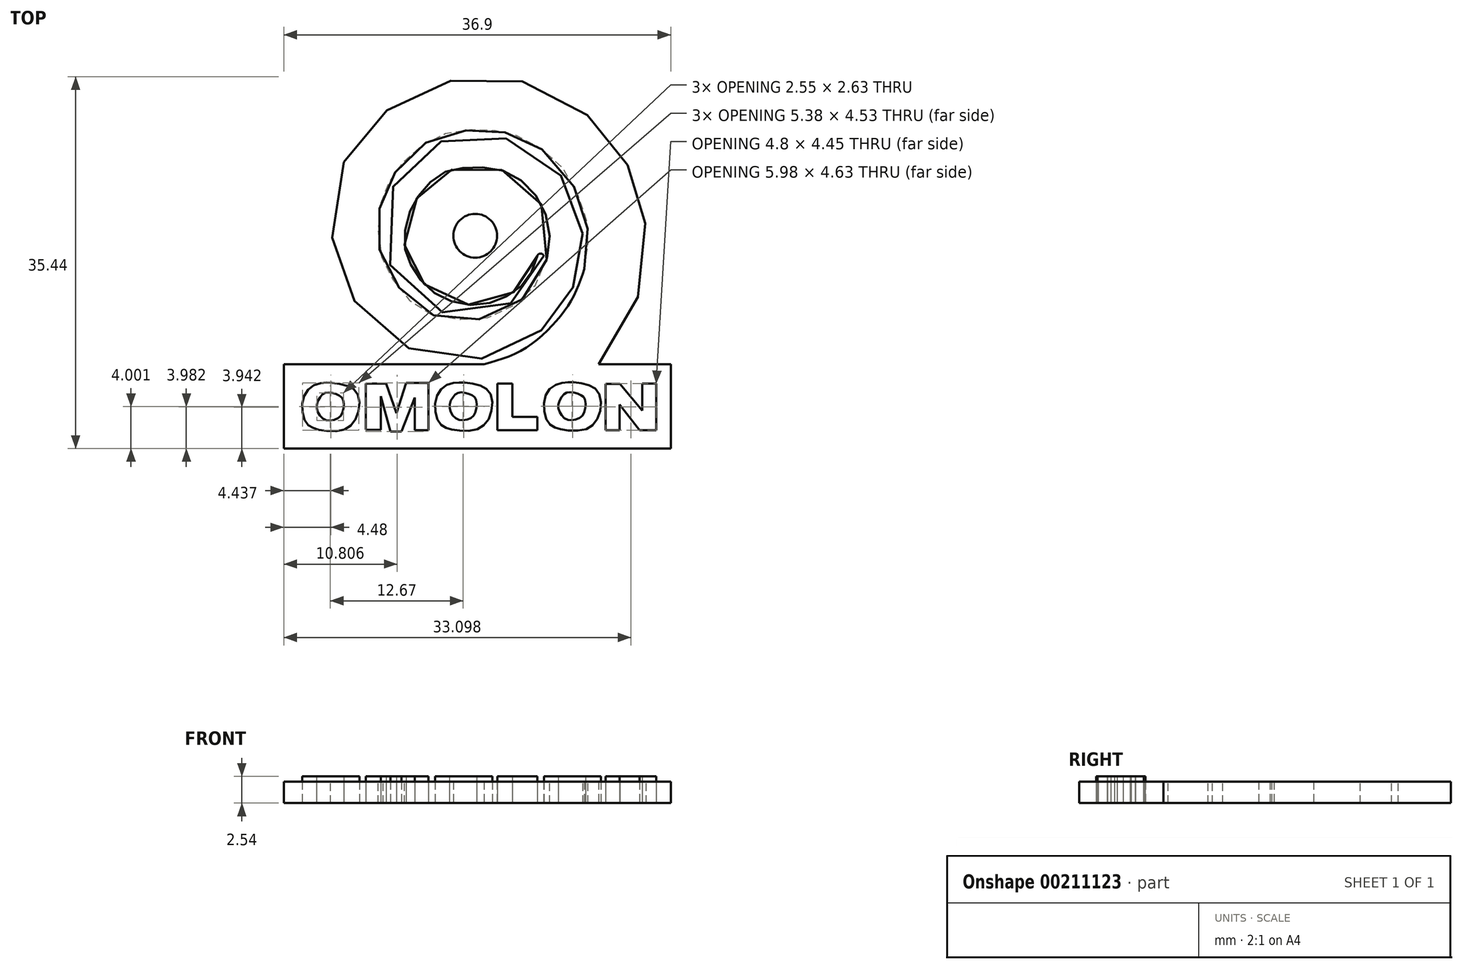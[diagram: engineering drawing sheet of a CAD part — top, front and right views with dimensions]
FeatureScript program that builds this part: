
annotation { "Feature Type Name" : "Feature", "Feature Type Description" : "" }
export const myFeature = defineFeature(function(context is Context, id is Id, definition is map)
    precondition{}
    {
        {
            var Q0;
            Q0=qCreatedBy(makeId("Top.planeOp"),FACE);
            var sketch = newSketch(context, id + "F0", { "sketchPlane" : qUnion([Q0])});
            skLineSegment(sketch, "E0.bottom", {"start": v(15, 8.8) * mm, "end": v(51.89, 8.8) * mm});
            skLineSegment(sketch, "E0.top", {"start": v(15, 0.75) * mm, "end": v(51.89, 0.75) * mm});
            skLineSegment(sketch, "E0.left", {"start": v(15, 8.8) * mm, "end": v(15, 0.75) * mm});
            skLineSegment(sketch, "E0.right", {"start": v(51.89, 8.8) * mm, "end": v(51.89, 0.75) * mm});
            skFitSpline(sketch, "E1", {"points": [v(34.07, 8.8) * mm, v(37.55, 10.04) * mm, v(40.6, 12.5) * mm, v(42.57, 15.18) * mm, v(43.65, 17.88) * mm], "startDerivative": vector(13.76, 3.77) * mm, "endDerivative": vector(4.03, 11.91) * mm});
            skFitSpline(sketch, "E2", {"points": [v(43.65, 17.88) * mm, v(43.94, 19.57) * mm, v(43.97, 21.74) * mm, v(43.65, 23.34) * mm, v(42.44, 26.15) * mm, v(40.7, 28.46) * mm, v(38.38, 29.96) * mm, v(36.75, 30.74) * mm, v(35.25, 31.02) * mm, v(33.55, 31.17) * mm, v(31.27, 30.92) * mm, v(29.35, 30.38) * mm, v(27.35, 28.96) * mm, v(25.9, 27.5) * mm, v(24.97, 26.04) * mm, v(24.22, 24.3) * mm, v(24.04, 22.13) * mm, v(24, 20.35) * mm, v(24.76, 17.88) * mm, v(25.79, 16.33) * mm, v(27.32, 14.55) * mm, v(29.42, 13.4) * mm, v(32.02, 13.05) * mm, v(34.3, 13.2) * mm, v(36.93, 14.37) * mm, v(38.81, 16.11) * mm, v(39.99, 18.5) * mm, v(40.2, 22.27) * mm, v(38.56, 25.4) * mm, v(35.9, 27.25) * mm, v(32.62, 27.54) * mm, v(30.2, 27.04) * mm, v(28.2, 25.3) * mm, v(27, 23.3) * mm, v(26.5, 20.28) * mm, v(27.14, 18.21) * mm, v(28.7, 16.11) * mm, v(31.13, 14.73) * mm, v(34.08, 14.51) * mm, v(36.5, 15.4) * mm, v(38.28, 17) * mm, v(39.17, 19.1) * mm], "startDerivative": vector(16.2, 77.75) * mm, "endDerivative": vector(29.34, 92.95) * mm});
            skFitSpline(sketch, "E3", {"points": [v(39.78, 19.1) * mm, v(39.37, 18) * mm, v(38.54, 16.46) * mm, v(37.25, 15.08) * mm, v(35.63, 14.04) * mm, v(33.6, 13.56) * mm, v(30.94, 13.54) * mm, v(27.94, 14.72) * mm, v(26.2, 16.38) * mm, v(25.15, 18.2) * mm, v(24.49, 21.47) * mm, v(24.8, 24.4) * mm, v(26.1, 26.84) * mm, v(27.37, 28.41) * mm, v(29.23, 29.68) * mm, v(30.85, 30.3) * mm, v(32.84, 30.5) * mm, v(35.1, 30.5) * mm, v(37.16, 30) * mm, v(39.17, 28.97) * mm, v(40.61, 27.72) * mm, v(42.22, 25.62) * mm, v(42.89, 24.22) * mm, v(43.35, 22.56) * mm, v(43.5, 20.7) * mm, v(43.46, 19.6) * mm, v(43.25, 18.14) * mm, v(42.7, 16.44) * mm, v(42.26, 15.49) * mm, v(41.59, 14.38) * mm, v(40.55, 13.05) * mm, v(39.61, 12.08) * mm, v(38, 10.83) * mm, v(36.4, 10.09) * mm, v(33.97, 9.34) * mm, v(31.22, 9.25) * mm, v(29.18, 9.43) * mm, v(26.07, 10.77) * mm, v(23.86, 12.48) * mm, v(22.42, 14) * mm, v(21.14, 15.67) * mm, v(20.28, 17.69) * mm, v(19.71, 20.21) * mm, v(19.55, 21.56) * mm, v(19.54, 24.45) * mm, v(20.58, 27.77) * mm, v(21.73, 29.82) * mm, v(23.28, 31.61) * mm, v(24.7, 32.89) * mm, v(26.7, 34.25) * mm, v(29.04, 35.32) * mm, v(31.14, 35.85) * mm, v(32.75, 36.13) * mm, v(35.65, 36.12) * mm, v(38.67, 35.44) * mm, v(41.26, 34.23) * mm, v(43.25, 33.04) * mm, v(44.85, 31.73) * mm, v(46.06, 30.34) * mm, v(47.21, 28.74) * mm, v(48.27, 26.74) * mm, v(48.96, 24.88) * mm, v(49.3, 23.52) * mm, v(49.47, 21.64) * mm, v(49.53, 18.55) * mm, v(49.07, 16.11) * mm, v(48.27, 14) * mm, v(47.06, 11.58) * mm, v(45.01, 8.8) * mm], "startDerivative": vector(-32.7, -97.66) * mm, "endDerivative": vector(-119.4, -150.7) * mm});
            skCircle(sketch, "E4", {"center": v(33.24, 21.03) * mm, "radius": 2.09 * mm});
            skArc(sketch, "E5", {"start": v(39.78, 19.1) * mm, "mid": v(39.47, 19.34) * mm, "end": v(39.17, 19.1) * mm});
            skLineSegment(sketch, "E6", {"start": v(22.8, 2.56) * mm, "end": v(22.8, 6.93) * mm});
            skLineSegment(sketch, "E7", {"start": v(22.8, 6.93) * mm, "end": v(24.76, 6.93) * mm});
            skLineSegment(sketch, "E8", {"start": v(24.76, 6.93) * mm, "end": v(25.72, 4.12) * mm});
            skLineSegment(sketch, "E9", {"start": v(25.72, 4.12) * mm, "end": v(26.65, 7) * mm});
            skLineSegment(sketch, "E10", {"start": v(26.65, 7) * mm, "end": v(28.78, 7) * mm});
            skLineSegment(sketch, "E11", {"start": v(28.78, 7) * mm, "end": v(28.78, 2.49) * mm});
            skLineSegment(sketch, "E12", {"start": v(28.78, 2.49) * mm, "end": v(27.47, 2.49) * mm});
            skLineSegment(sketch, "E13", {"start": v(27.47, 2.49) * mm, "end": v(27.47, 5.62) * mm});
            skLineSegment(sketch, "E14", {"start": v(27.47, 5.62) * mm, "end": v(26.22, 2.38) * mm});
            skLineSegment(sketch, "E15", {"start": v(26.22, 2.38) * mm, "end": v(25.16, 2.38) * mm});
            skLineSegment(sketch, "E16", {"start": v(25.16, 2.38) * mm, "end": v(24.23, 5.72) * mm});
            skLineSegment(sketch, "E17", {"start": v(24.23, 5.72) * mm, "end": v(24.23, 2.52) * mm});
            skLineSegment(sketch, "E18", {"start": v(24.23, 2.52) * mm, "end": v(22.8, 2.56) * mm});
            skLineSegment(sketch, "E19", {"start": v(35.37, 6.93) * mm, "end": v(35.37, 2.49) * mm});
            skLineSegment(sketch, "E20", {"start": v(35.37, 2.49) * mm, "end": v(39.17, 2.49) * mm});
            skLineSegment(sketch, "E21", {"start": v(39.17, 2.49) * mm, "end": v(39.17, 3.77) * mm});
            skLineSegment(sketch, "E22", {"start": v(39.17, 3.77) * mm, "end": v(36.8, 3.77) * mm});
            skLineSegment(sketch, "E23", {"start": v(36.8, 3.77) * mm, "end": v(36.8, 6.93) * mm});
            skLineSegment(sketch, "E24", {"start": v(36.8, 6.93) * mm, "end": v(35.37, 6.93) * mm});
            skLineSegment(sketch, "E25", {"start": v(45.69, 6.9) * mm, "end": v(45.69, 2.49) * mm});
            skLineSegment(sketch, "E26", {"start": v(45.69, 2.49) * mm, "end": v(47, 2.49) * mm});
            skLineSegment(sketch, "E27", {"start": v(47, 2.49) * mm, "end": v(47, 4.94) * mm});
            skLineSegment(sketch, "E28", {"start": v(47, 4.94) * mm, "end": v(48.92, 2.49) * mm});
            skLineSegment(sketch, "E29", {"start": v(48.92, 2.49) * mm, "end": v(50.49, 2.49) * mm});
            skLineSegment(sketch, "E30", {"start": v(50.49, 2.49) * mm, "end": v(50.49, 6.93) * mm});
            skLineSegment(sketch, "E31", {"start": v(50.49, 6.93) * mm, "end": v(49.18, 6.93) * mm});
            skLineSegment(sketch, "E32", {"start": v(49.18, 6.93) * mm, "end": v(49.18, 4.37) * mm});
            skLineSegment(sketch, "E33", {"start": v(49.18, 4.37) * mm, "end": v(47.04, 6.9) * mm});
            skLineSegment(sketch, "E34", {"start": v(47.04, 6.9) * mm, "end": v(45.69, 6.9) * mm});
            skFitSpline(sketch, "E35", {"points": [v(19.6, 7.02) * mm, v(18.85, 7.02) * mm, v(17.85, 6.79) * mm, v(17, 5.96) * mm, v(16.75, 4.46) * mm, v(17.15, 3.19) * mm, v(17.77, 2.72) * mm, v(18.68, 2.49) * mm, v(20.52, 2.49) * mm, v(21.64, 3.21) * mm, v(22.19, 4.75) * mm, v(21.9, 6.17) * mm, v(20.96, 6.76) * mm, v(19.6, 7.02) * mm]});
            skFitSpline(sketch, "E36", {"points": [v(19.6, 6.05) * mm, v(18.93, 6.05) * mm, v(18.49, 5.69) * mm, v(18.13, 4.88) * mm, v(18.28, 4.16) * mm, v(18.83, 3.53) * mm, v(19.6, 3.44) * mm, v(20.37, 3.8) * mm, v(20.69, 4.59) * mm, v(20.65, 5.43) * mm, v(20.3, 5.8) * mm, v(19.6, 6.05) * mm]});
            skFitSpline(sketch, "E37", {"points": [v(32.28, 7.04) * mm, v(31.52, 7.04) * mm, v(30.52, 6.8) * mm, v(29.68, 5.98) * mm, v(29.42, 4.48) * mm, v(29.82, 3.21) * mm, v(30.44, 2.74) * mm, v(31.35, 2.5) * mm, v(33.19, 2.5) * mm, v(34.3, 3.23) * mm, v(34.86, 4.78) * mm, v(34.56, 6.2) * mm, v(33.63, 6.79) * mm, v(32.28, 7.04) * mm]});
            skFitSpline(sketch, "E38", {"points": [v(32.28, 6.07) * mm, v(31.6, 6.07) * mm, v(31.16, 5.7) * mm, v(30.8, 4.9) * mm, v(30.95, 4.18) * mm, v(31.5, 3.55) * mm, v(32.28, 3.46) * mm, v(33.04, 3.82) * mm, v(33.36, 4.6) * mm, v(33.32, 5.45) * mm, v(32.98, 5.81) * mm, v(32.28, 6.07) * mm]});
            skFitSpline(sketch, "E39", {"points": [v(42.65, 7.06) * mm, v(41.9, 7.06) * mm, v(40.9, 6.83) * mm, v(40.05, 6) * mm, v(39.8, 4.5) * mm, v(40.2, 3.23) * mm, v(40.81, 2.77) * mm, v(41.72, 2.53) * mm, v(43.56, 2.53) * mm, v(44.68, 3.25) * mm, v(45.23, 4.8) * mm, v(44.94, 6.21) * mm, v(44, 6.8) * mm, v(42.65, 7.06) * mm]});
            skFitSpline(sketch, "E40", {"points": [v(42.65, 6.09) * mm, v(41.98, 6.09) * mm, v(41.53, 5.73) * mm, v(41.17, 4.92) * mm, v(41.32, 4.2) * mm, v(41.87, 3.57) * mm, v(42.65, 3.49) * mm, v(43.42, 3.84) * mm, v(43.73, 4.63) * mm, v(43.7, 5.47) * mm, v(43.35, 5.83) * mm, v(42.65, 6.09) * mm]});
            skSolve(sketch);
        }
        {
            var Q0;
            Q0=makeQuery(id+"F0.imprint","IMPRINT",FACE,{"disambiguationData":[TD([[makeQuery(id+"F0.imprint","IMPRINT",EDGE,{"derivedFrom":sQuery(id+"F0.wireOp",EDGE,"E0.top")}),1.0]])]});
            var Q1;
            {var subQ1=sQuery(id+"F0.wireOp",EDGE,"E1");Q1=makeQuery(id+"F0.imprint","IMPRINT",FACE,{"disambiguationData":[TD([[makeQuery(id+"F0.imprint","IMPRINT",EDGE,{"derivedFrom":subQ1}),-1.0]])]});}
            var Q2;
            Q2=makeQuery(id+"F0.imprint","IMPRINT",FACE,{"disambiguationData":[TD([[makeQuery(id+"F0.imprint","IMPRINT",EDGE,{"derivedFrom":sQuery(id+"F0.wireOp",EDGE,"E36")}),1.0]])]});
            var Q3;
            Q3=makeQuery(id+"F0.imprint","IMPRINT",FACE,{"disambiguationData":[TD([[makeQuery(id+"F0.imprint","IMPRINT",EDGE,{"derivedFrom":sQuery(id+"F0.wireOp",EDGE,"E38")}),1.0]])]});
            var Q4;
            Q4=makeQuery(id+"F0.imprint","IMPRINT",FACE,{"disambiguationData":[TD([[makeQuery(id+"F0.imprint","IMPRINT",EDGE,{"derivedFrom":sQuery(id+"F0.wireOp",EDGE,"E40")}),1.0]])]});
            var Q5;
            Q5=makeQuery(id+"F0.imprint","IMPRINT",FACE,{"disambiguationData":[TD([[makeQuery(id+"F0.imprint","IMPRINT",EDGE,{"derivedFrom":sQuery(id+"F0.wireOp",EDGE,"E4")}),1.0]])]});
            extrude(context, id + "F1", {"entities" : qUnion([Q0, Q1, Q2, Q3, Q4, Q5]), "depth" : 2.03 * mm});
        }
        {
            var Q0;
            Q0=makeQuery(id+"F0.imprint","IMPRINT",FACE,{"disambiguationData":[TD([[makeQuery(id+"F0.imprint","IMPRINT",EDGE,{"derivedFrom":sQuery(id+"F0.wireOp",EDGE,"E35")}),1.0]])]});
            var Q1;
            Q1=makeQuery(id+"F0.imprint","IMPRINT",FACE,{"disambiguationData":[TD([[makeQuery(id+"F0.imprint","IMPRINT",EDGE,{"derivedFrom":sQuery(id+"F0.wireOp",EDGE,"E6")}),-1.0]])]});
            var Q2;
            Q2=makeQuery(id+"F0.imprint","IMPRINT",FACE,{"disambiguationData":[TD([[makeQuery(id+"F0.imprint","IMPRINT",EDGE,{"derivedFrom":sQuery(id+"F0.wireOp",EDGE,"E37")}),1.0]])]});
            var Q3;
            Q3=makeQuery(id+"F0.imprint","IMPRINT",FACE,{"disambiguationData":[TD([[makeQuery(id+"F0.imprint","IMPRINT",EDGE,{"derivedFrom":sQuery(id+"F0.wireOp",EDGE,"E19")}),1.0]])]});
            var Q4;
            Q4=makeQuery(id+"F0.imprint","IMPRINT",FACE,{"disambiguationData":[TD([[makeQuery(id+"F0.imprint","IMPRINT",EDGE,{"derivedFrom":sQuery(id+"F0.wireOp",EDGE,"E39")}),1.0]])]});
            var Q5;
            Q5=makeQuery(id+"F0.imprint","IMPRINT",FACE,{"disambiguationData":[TD([[makeQuery(id+"F0.imprint","IMPRINT",EDGE,{"derivedFrom":sQuery(id+"F0.wireOp",EDGE,"E25")}),1.0]])]});
            extrude(context, id + "F2", {"entities" : qUnion([Q0, Q1, Q2, Q3, Q4, Q5]), "depth" : 2.54 * mm});
        }
    });
